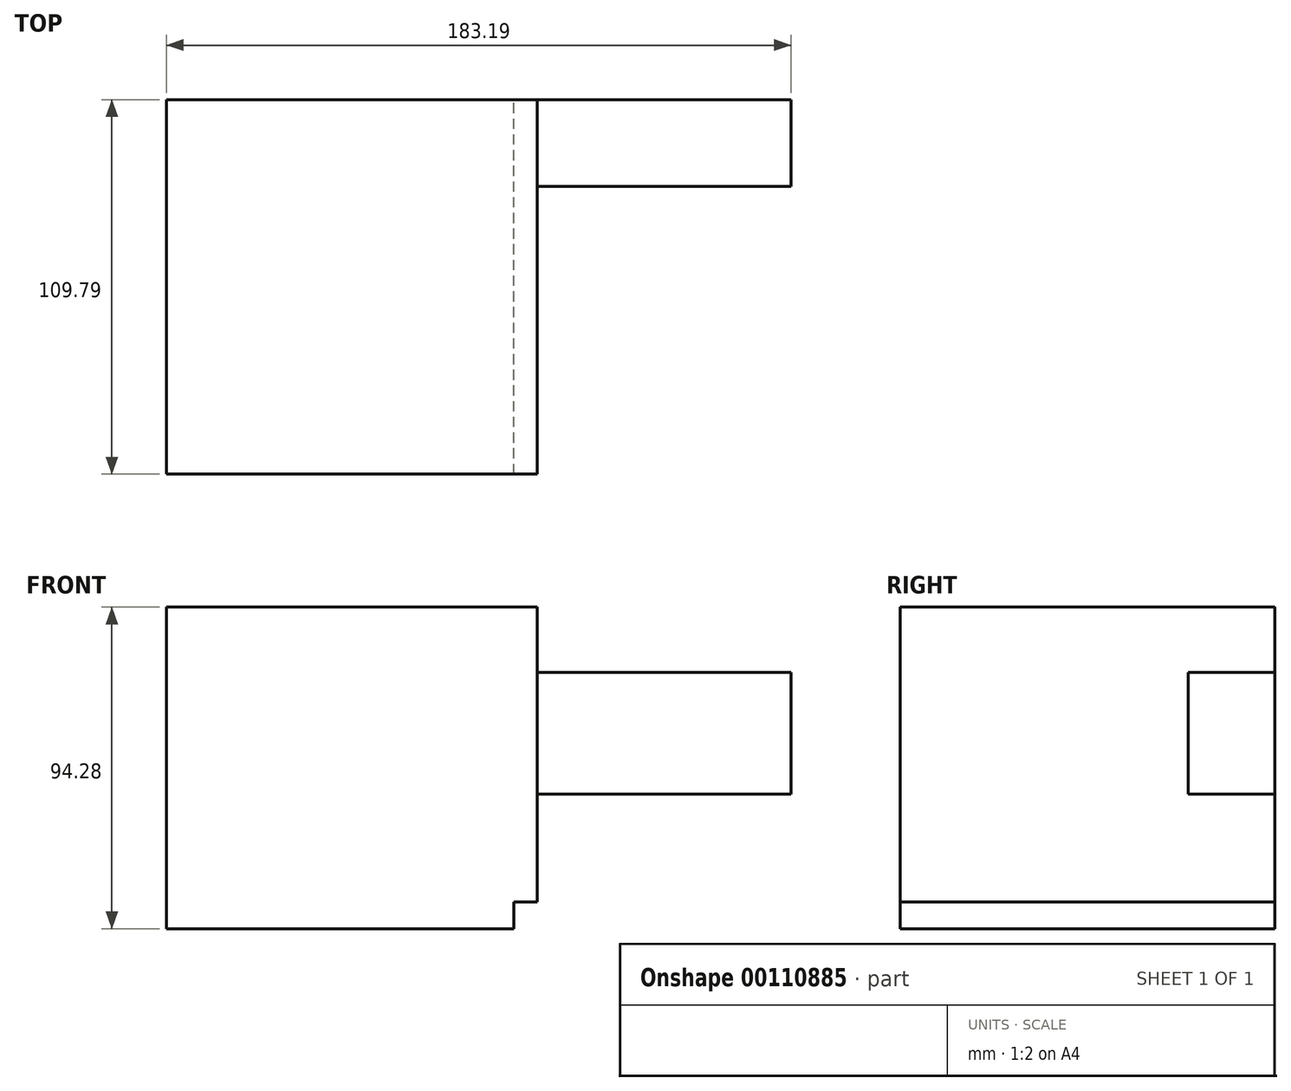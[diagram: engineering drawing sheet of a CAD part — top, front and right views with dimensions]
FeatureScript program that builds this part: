
annotation { "Feature Type Name" : "Feature", "Feature Type Description" : "" }
export const myFeature = defineFeature(function(context is Context, id is Id, definition is map)
    precondition{}
    {
        {
            var Q0;
            Q0=qCreatedBy(makeId("Front.planeOp"),FACE);
            var sketch = newSketch(context, id + "F0", { "sketchPlane" : qUnion([Q0])});
            skLineSegment(sketch, "E0.bottom", {"start": v(36.27, 55.97) * mm, "end": v(-40.84, 55.97) * mm});
            skLineSegment(sketch, "E0.top", {"start": v(36.27, 20.28) * mm, "end": v(-40.84, 20.28) * mm});
            skLineSegment(sketch, "E0.left", {"start": v(36.27, 55.97) * mm, "end": v(36.27, 20.28) * mm});
            skLineSegment(sketch, "E0.right", {"start": v(-40.84, 55.97) * mm, "end": v(-40.84, 20.28) * mm});
            skSolve(sketch);
        }
        {
            var Q0;
            Q0=makeQuery(id+"F0.imprint","IMPRINT",FACE,{"disambiguationData":[TD([[makeQuery(id+"F0.imprint","IMPRINT",EDGE,{"derivedFrom":sQuery(id+"F0.wireOp",EDGE,"E0.bottom")}),1.0]])]});
            extrude(context, id + "F1", {"entities" : qUnion([Q0]), "depth" : 25.4 * mm});
        }
        {
            var Q0;
            Q0=qCreatedBy(makeId("Front.planeOp"),FACE);
            var sketch = newSketch(context, id + "F2", { "sketchPlane" : qUnion([Q0])});
            skLineSegment(sketch, "E1.bottom", {"start": v(-45.1, -30.15) * mm, "end": v(37.06, -30.15) * mm});
            skLineSegment(sketch, "E1.top", {"start": v(-45.1, -11.38) * mm, "end": v(37.06, -11.38) * mm});
            skLineSegment(sketch, "E1.left", {"start": v(-45.1, -30.15) * mm, "end": v(-45.1, -11.38) * mm});
            skLineSegment(sketch, "E1.right", {"start": v(37.06, -30.15) * mm, "end": v(37.06, -11.38) * mm});
            skSolve(sketch);
        }
        {
            var Q0;
            Q0=makeQuery(id+"F2.imprint","IMPRINT",FACE,{"disambiguationData":[TD([[makeQuery(id+"F2.imprint","IMPRINT",EDGE,{"derivedFrom":sQuery(id+"F2.wireOp",EDGE,"E1.bottom")}),1.0]])]});
            var sketch = newSketch(context, id + "F3", { "sketchPlane" : qUnion([Q0])});
            skLineSegment(sketch, "E2.bottom", {"start": v(-15.9, -27.15) * mm, "end": v(-15.53, -27.15) * mm});
            skLineSegment(sketch, "E2.top", {"start": v(-15.9, -19.31) * mm, "end": v(-15.53, -19.31) * mm});
            skLineSegment(sketch, "E2.left", {"start": v(-15.9, -27.15) * mm, "end": v(-15.9, -19.31) * mm});
            skLineSegment(sketch, "E2.right", {"start": v(-15.53, -27.15) * mm, "end": v(-15.53, -19.31) * mm});
            skLineSegment(sketch, "E3.bottom", {"start": v(-38.16, -19.16) * mm, "end": v(-146.92, -19.16) * mm});
            skLineSegment(sketch, "E3.top", {"start": v(-38.16, 75.12) * mm, "end": v(-146.92, 75.12) * mm});
            skLineSegment(sketch, "E3.left", {"start": v(-38.16, -19.16) * mm, "end": v(-38.16, 75.12) * mm});
            skLineSegment(sketch, "E3.right", {"start": v(-146.92, -19.16) * mm, "end": v(-146.92, 75.12) * mm});
            skSolve(sketch);
        }
        {
            var Q0;
            {var subQ2=sQuery(id+"F3.wireOp",EDGE,"E3.top");Q0=makeQuery(id+"F3.imprint","IMPRINT",FACE,{"disambiguationData":[TD([[makeQuery(id+"F3.imprint","IMPRINT",EDGE,{"derivedFrom":subQ2}),1.0]])]});}
            extrude(context, id + "F4", {"entities" : qUnion([Q0]), "operationType" : NewBodyOperationType.ADD, "depth" : 109.8 * mm});
        }
    });
